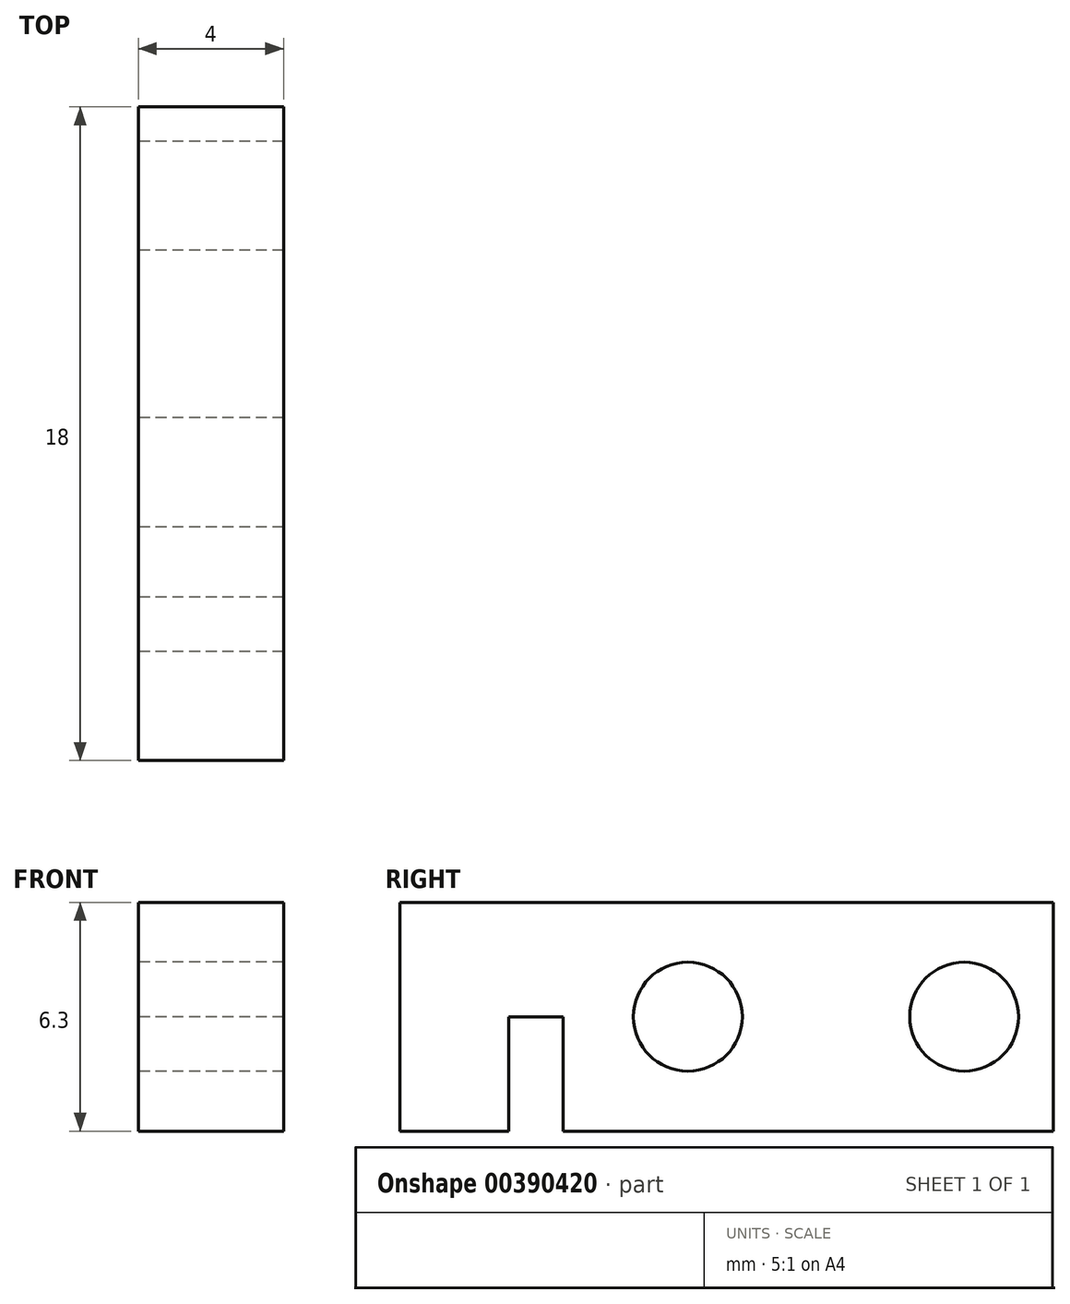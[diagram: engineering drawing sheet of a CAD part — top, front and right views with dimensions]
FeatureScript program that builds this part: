
annotation { "Feature Type Name" : "Feature", "Feature Type Description" : "" }
export const myFeature = defineFeature(function(context is Context, id is Id, definition is map)
    precondition{}
    {
        {
            var Q0;
            Q0=qCreatedBy(makeId("Front.planeOp"),FACE);
            var sketch = newSketch(context, id + "F0", { "sketchPlane" : qUnion([Q0])});
            skLineSegment(sketch, "E0.bottom", {"start": v(2, 3.15) * mm, "end": v(-2, 3.15) * mm});
            skLineSegment(sketch, "E0.top", {"start": v(2, -3.15) * mm, "end": v(-2, -3.15) * mm});
            skLineSegment(sketch, "E0.left", {"start": v(2, 3.15) * mm, "end": v(2, -3.15) * mm});
            skLineSegment(sketch, "E0.right", {"start": v(-2, 3.15) * mm, "end": v(-2, -3.15) * mm});
            skPoint(sketch, "E0.middle", {"position": v(0, 0) * mm});
            skSolve(sketch);
        }
        {
            var Q0;
            Q0=makeQuery(id+"F0.imprint","IMPRINT",FACE,{"disambiguationData":[TD([[makeQuery(id+"F0.imprint","IMPRINT",EDGE,{"derivedFrom":sQuery(id+"F0.wireOp",EDGE,"E0.bottom")}),1.0]])]});
            extrude(context, id + "F1", {"entities" : qUnion([Q0]), "depth" : 18 * mm});
        }
        {
            var Q0;
            Q0=makeQuery(id+"F1.opExtrude","SWEPT_FACE",FACE,{"disambiguationData":[OSD([sQuery(id+"F0.wireOp",EDGE,"E0.right")])]});
            var sketch = newSketch(context, id + "F2", { "sketchPlane" : qUnion([Q0])});
            skLineSegment(sketch, "E1.bottom", {"start": v(13.5, 0) * mm, "end": v(15, 0) * mm});
            skLineSegment(sketch, "E1.top", {"start": v(13.5, -3.15) * mm, "end": v(15, -3.15) * mm});
            skLineSegment(sketch, "E1.left", {"start": v(13.5, 0) * mm, "end": v(13.5, -3.15) * mm});
            skLineSegment(sketch, "E1.right", {"start": v(15, 0) * mm, "end": v(15, -3.15) * mm});
            skSolve(sketch);
        }
        {
            var Q0;
            Q0=makeQuery(id+"F2.imprint","IMPRINT",FACE,{"disambiguationData":[TD([[makeQuery(id+"F2.imprint","IMPRINT",EDGE,{"derivedFrom":sQuery(id+"F2.wireOp",EDGE,"E1.bottom")}),-1.0]])]});
            extrude(context, id + "F3", {"entities" : qUnion([Q0]), "operationType" : NewBodyOperationType.REMOVE, "oppositeDirection" : true, "depth" : 25 * mm});
        }
        {
            var Q0;
            Q0=makeQuery(id+"F1.opExtrude","SWEPT_FACE",FACE,{"disambiguationData":[OSD([sQuery(id+"F0.wireOp",EDGE,"E0.right")])]});
            var sketch = newSketch(context, id + "F4", { "sketchPlane" : qUnion([Q0])});
            skCircle(sketch, "E2", {"center": v(2.45, 0) * mm, "radius": 1.5 * mm});
            skCircle(sketch, "E3", {"center": v(10.06, 0) * mm, "radius": 1.5 * mm});
            skSolve(sketch);
        }
        {
            var Q0;
            Q0=makeQuery(id+"F4.imprint","IMPRINT",FACE,{"disambiguationData":[TD([[makeQuery(id+"F4.imprint","IMPRINT",EDGE,{"derivedFrom":sQuery(id+"F4.wireOp",EDGE,"E2")}),1.0]])]});
            var Q1;
            Q1=makeQuery(id+"F4.imprint","IMPRINT",FACE,{"disambiguationData":[TD([[makeQuery(id+"F4.imprint","IMPRINT",EDGE,{"derivedFrom":sQuery(id+"F4.wireOp",EDGE,"E3")}),1.0]])]});
            extrude(context, id + "F5", {"entities" : qUnion([Q0, Q1]), "operationType" : NewBodyOperationType.REMOVE, "oppositeDirection" : true, "depth" : 25 * mm});
        }
    });
